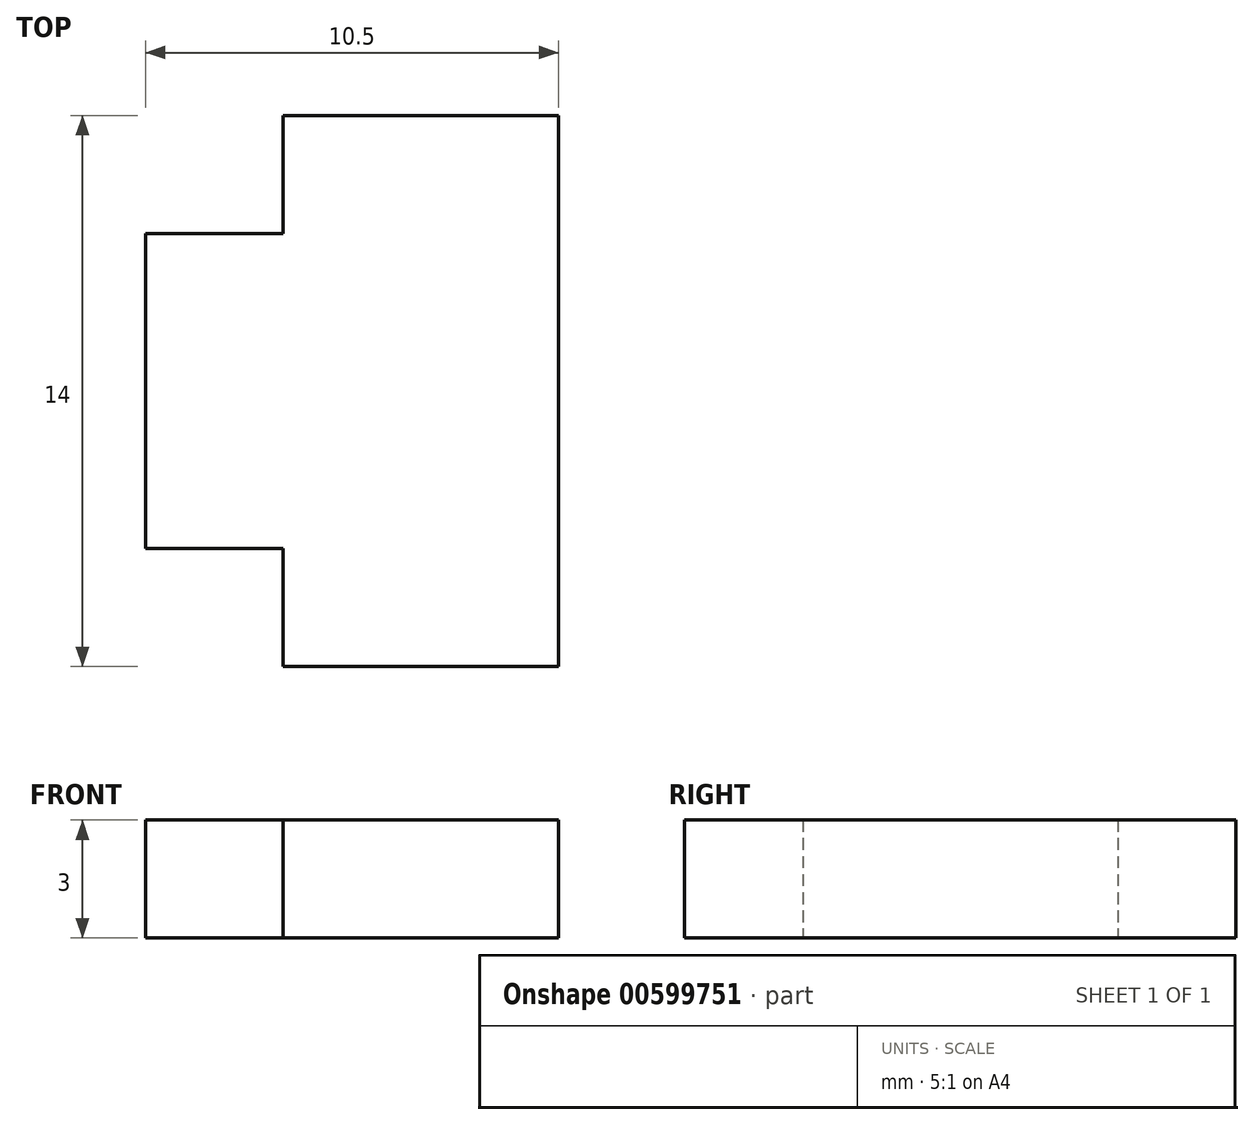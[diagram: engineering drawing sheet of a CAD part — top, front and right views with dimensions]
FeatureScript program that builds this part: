
annotation { "Feature Type Name" : "Feature", "Feature Type Description" : "" }
export const myFeature = defineFeature(function(context is Context, id is Id, definition is map)
    precondition{}
    {
        {
            var Q0;
            Q0=qCreatedBy(makeId("Top.planeOp"),FACE);
            var sketch = newSketch(context, id + "F0", { "sketchPlane" : qUnion([Q0])});
            skLineSegment(sketch, "E0.bottom", {"start": v(49.5, 7) * mm, "end": v(-49.5, 7) * mm});
            skLineSegment(sketch, "E0.top", {"start": v(49.5, -7) * mm, "end": v(-49.5, -7) * mm});
            skLineSegment(sketch, "E0.left", {"start": v(49.5, 7) * mm, "end": v(49.5, -7) * mm});
            skLineSegment(sketch, "E0.right", {"start": v(-49.5, 7) * mm, "end": v(-49.5, -7) * mm});
            skPoint(sketch, "E0.middle", {"position": v(0, 0) * mm});
            skLineSegment(sketch, "E1", {"start": v(42.5, 7) * mm, "end": v(42.5, 4) * mm});
            skLineSegment(sketch, "E2", {"start": v(42.5, 4) * mm, "end": v(46, 4) * mm});
            skLineSegment(sketch, "E3", {"start": v(46, 4) * mm, "end": v(46, -4) * mm});
            skLineSegment(sketch, "E4", {"start": v(46, -4) * mm, "end": v(42.5, -4) * mm});
            skLineSegment(sketch, "E5", {"start": v(42.5, -4) * mm, "end": v(42.5, -7) * mm});
            skLineSegment(sketch, "E6", {"start": v(-42.5, 7) * mm, "end": v(-42.5, 4) * mm});
            skLineSegment(sketch, "E7", {"start": v(-42.5, 4) * mm, "end": v(-46, 4) * mm});
            skLineSegment(sketch, "E8", {"start": v(-46, 4) * mm, "end": v(-46, -4) * mm});
            skLineSegment(sketch, "E9", {"start": v(-46, -4) * mm, "end": v(-42.5, -4) * mm});
            skLineSegment(sketch, "E10", {"start": v(-42.5, -4) * mm, "end": v(-42.5, -7) * mm});
            skLineSegment(sketch, "E11", {"start": v(-35.5, 7) * mm, "end": v(-35.5, -7) * mm});
            skSolve(sketch);
        }
        {
            var Q0;
            {var subQ0=sQuery(id+"F0.wireOp",EDGE,"E6");Q0=makeQuery(id+"F0.imprint","IMPRINT",FACE,{"disambiguationData":[TD([[makeQuery(id+"F0.imprint","IMPRINT",EDGE,{"derivedFrom":subQ0}),1.0]])]});}
            extrude(context, id + "F1", {"entities" : qUnion([Q0]), "depth" : 3 * mm, "offsetDistance" : 25 * mm});
        }
    });
